# Revit family: CIVIC WALL MOUNT 90MM BOTTLE FILLER
name_source: partatom
category: Plumbing Fixtures
units: mm (PartAtom-declared; Revit-internal decimal feet)

## family parameters
Cut with Voids When Loaded = Yes
Host = Face
OmniClass Number = 23.45.55.14
OmniClass Title = Single Faucets
Part Type = Normal
Room Calculation Point = No
Round Connector Dimension = Use Diameter
Shared = No

## types (1)
- CIVIC WALL MOUNT 90MM BOTTLE FILLER
    Assembly Code = D2020300
    Base_Material = GWA_Metal-Chrome
    CW Connection = Yes
    Default Elevation = 0 mm  [stored 0 ft]
    Description = CIVIC WALL MOUNT 90MM BOTTLE FILLER
    HW Connection = No
    Indicator_Colour = GWA-Plastic-Blue
    Manufacturer = GWA Bathrooms & Kitchens
    Model = 96419C6A
    URL = https://www.caroma.com.au
    Vent Connection = No
    Waste Connection = No

note: [stored X ft] marks values corroborated as IEEE doubles in the binary element streams (Revit-internal decimal feet)

## geometry (parser evidence)
native form markers: Sweep x2
no freeform markers — native parametric forms only
